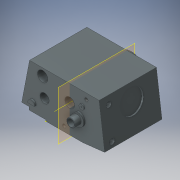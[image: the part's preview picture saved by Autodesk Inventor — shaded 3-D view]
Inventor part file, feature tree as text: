
AUTODESK INVENTOR PART (.ipt)
format: ipt  version: 2016 (Build 200138000, 138)  size: 352,768 bytes
history: native  units: in
note: dims shown in document units (in); Inventor stores cm internally (conversion verified against a paired STEP export)
features: sketch x19, extrude x17, fillet x2, thread x2, chamfer x1, hole x1, plane x1, other x1
ambient origin geometry x8: Origin, YZ Plane, XZ Plane, XY Plane, X Axis, Y Axis, Z Axis, Center Point
bodies: Solid1 (feature_tree)
feature tree (44):
  extrude  "Extrusion1"  Depth=10.4921in
  sketch  "Sketch3"  dims[d7=10.0in d8=0.5669in]
  extrude  "Extrusion2"  Depth=0.5669in
  extrude  "Extrusion3"  Depth=0.694in
  extrude  "Extrusion4"  Depth=0.7087in
  extrude  "Extrusion5"  Depth=0.0787in
  extrude  "Extrusion6"  Depth=13.4646in TaperAngle=0.0deg
  fillet  "Fillet1"  Radius=5.5118in
  fillet  "Fillet2"  Radius=6.2992in
  extrude  "Extrusion7"  Depth=2.7559in
  thread  "Thread1"  [1 undecoded]
  sketch  "Sketch9"  dims[d30=0.3937in d31=0.0in d34=1.1811in]
  extrude  "Extrusion8"  Depth=1.1811in
  extrude  "Extrusion9"  Depth=1.7717in
  extrude  "Extrusion10"  Depth=1.2106in
  chamfer  "Chamfer1"  Distance=2.3622in
  extrude  "Extrusion11"  Depth=0.748in
  extrude  "Extrusion12"  Depth=1.0236in TaperAngle=0.0deg
  extrude  "Extrusion13"  Depth=1.0236in TaperAngle=0.0deg
  extrude  "Extrusion14"  Depth=1.378in
  hole  "Hole1"  [1 undecoded]
  extrude  "Extrusion15"  Depth=0.0787in
  extrude  "Extrusion16"  Depth=0.7874in
  extrude  "Extrusion17"  Depth=0.3937in TaperAngle=0.0deg
  thread  "Thread2"  [1 undecoded]
  plane  "Work Plane2"
  sketch  "Sketch1"  dims[d0=8.6614in d1=10.4921in]
  sketch  "Sketch4"  dims[d9=9.6457in d10=0.694in]
  sketch  "Sketch5"  dims[d11=1.7717in d12=0.7087in]
  sketch  "Sketch6"  dims[d14=16.3386in d15=0.0787in]
  sketch  "Sketch7"  dims[d16=0.0787in d17=13.4646in d18=0.0in d22=5.5118in d26=6.2992in]
  sketch  "Sketch8"  dims[d27=2.7559in d28=3.6024in d29=2.7559in]
  sketch  "Sketch10"  dims[d37=1.7717in d38=2.0079in]
  sketch  "Sketch11"  dims[d39=1.2402in d42=1.2106in]
  sketch  "Sketch12"  dims[d43=1.8799in d44=2.3622in d45=0.0in]
  sketch  "Sketch13"  dims[d49=6.3386in d50=0.748in]
  sketch  "Sketch14"  dims[d52=7.4213in d53=1.0236in d54=0.0in]
  sketch  "Sketch15"  dims[d55=2.2835in d56=1.0236in d57=0.0in]
  sketch  "Sketch16"  dims[d69=0.7874in d70=1.378in]
  sketch  "Sketch17"  dims[d72=0.3937in d73=0.315in]
  sketch  "Sketch19"  dims[d75=0.2362in d76=0.0in d77=0.0787in]
  sketch  "Sketch20"  dims[d78=0.0787in d82=0.7874in]
  sketch  "Sketch21"  dims[d83=1.1811in d84=0.0in d85=0.3937in d86=0.0in d87=3.0118in d88=45.0deg d91=0.3937in d92=0.0in d93=2.0079in d94=1.6929in d95=1.4961in d96=0.0in d97=1.9685in d98=0.0in d99=0.0787in d100=0.0787in d101=45.0deg d103=1.1811in d105=0.3937in d106=0.0in d107=5.9055in d108=5.9646in d109=90.0deg d110=2.7559in d111=7.4803in d112=90.0deg d113=0.3937in d114=0.0in d116=0.3937in d117=0.0in d118=2.9528in d120=3.2283in d121=1.1811in d122=0.1969in d123=0.0in d124=0.2559in d125=0.1181in d126=0.2362in d127=0.2559in d128=0.0787in d129=90.0deg d130=0.1969in d131=0.0in d132=6.6929in d133=90.0deg d134=1.7323in d135=2.4409in d136=0.7874in d137=0.0in d138=5.9055in d139=5.9646in d140=90.0deg d141=2.1654in d142=2.7559in d143=0.0in d144=0.9843in d145=1.3386in d146=0.7874in d147=0.7874in d148=0.0in d149=0.3937in d150=0.0in d151=0.0in]
  other  "Work Axis1"
note: 3 required parameter values undecoded (feature->parameter linkage not recoverable at this tier; creation-order binding heuristic only, values carry confidence <= 0.55)
